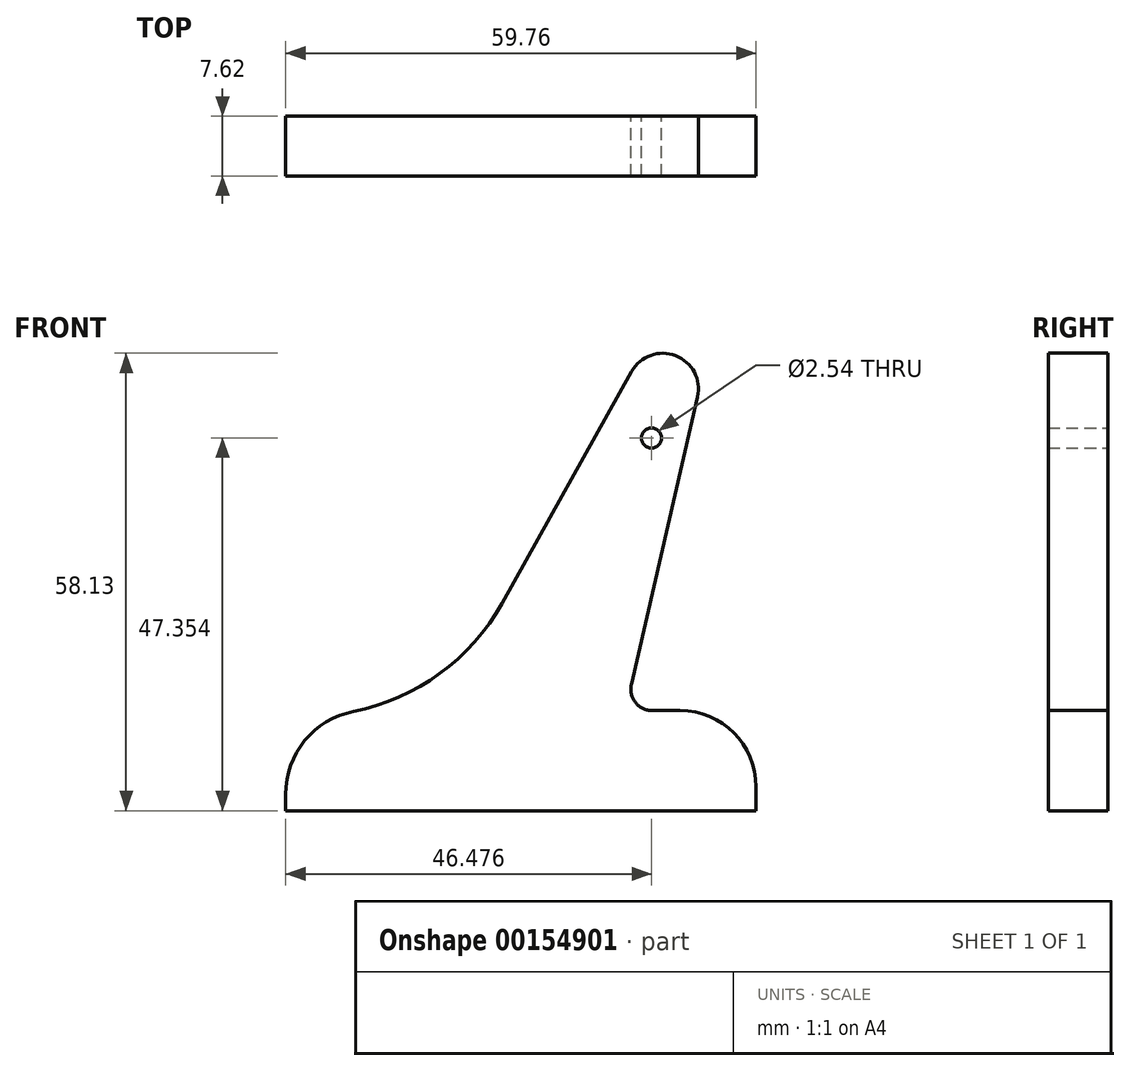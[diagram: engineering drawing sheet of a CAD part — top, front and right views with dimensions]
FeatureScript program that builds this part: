
annotation { "Feature Type Name" : "Feature", "Feature Type Description" : "" }
export const myFeature = defineFeature(function(context is Context, id is Id, definition is map)
    precondition{}
    {
        {
            var Q0;
            Q0=qCreatedBy(makeId("Front.planeOp"),FACE);
            var sketch = newSketch(context, id + "F0", { "sketchPlane" : qUnion([Q0])});
            skLineSegment(sketch, "E0", {"start": v(-31.95, 0) * mm, "end": v(0, 0) * mm});
            skLineSegment(sketch, "E1", {"start": v(0, 0) * mm, "end": v(27.81, 0) * mm});
            skLineSegment(sketch, "E2", {"start": v(-31.95, 0) * mm, "end": v(-31.95, 12.83) * mm});
            skLineSegment(sketch, "E3", {"start": v(-31.95, 12.83) * mm, "end": v(-12, 12.83) * mm});
            skLineSegment(sketch, "E4", {"start": v(-12, 12.83) * mm, "end": v(27.51, 83.55) * mm});
            skLineSegment(sketch, "E5", {"start": v(27.51, 83.55) * mm, "end": v(11.2, 12.72) * mm});
            skLineSegment(sketch, "E6", {"start": v(27.81, 0) * mm, "end": v(27.81, 12.72) * mm});
            skLineSegment(sketch, "E7", {"start": v(27.81, 12.72) * mm, "end": v(11.2, 12.72) * mm});
            skCircle(sketch, "E8", {"center": v(14.53, 47.35) * mm, "radius": 1.27 * mm});
            skSolve(sketch);
        }
        {
            var Q0;
            Q0=makeQuery(id+"F0.imprint","IMPRINT",FACE,{"disambiguationData":[TD([[makeQuery(id+"F0.imprint","IMPRINT",EDGE,{"derivedFrom":sQuery(id+"F0.wireOp",EDGE,"E0")}),1.0]])]});
            extrude(context, id + "F1", {"entities" : qUnion([Q0]), "depth" : 7.62 * mm});
        }
        {
            var Q0;
            Q0=makeQuery(id+"F1.opExtrude","SWEPT_EDGE",EDGE,{"disambiguationData":[OSD([sQuery(id+"F0.wireOp",EDGE,"E2"),sQuery(id+"F0.wireOp",EDGE,"E3")])]});
            fillet(context, id + "F2", {"entities" : qUnion([Q0]), "radius" : 10.73 * mm, "tangentPropagation" : true, "allowEdgeOverflow" : false});
        }
        {
            var Q0;
            Q0=makeQuery(id+"F1.opExtrude","SWEPT_EDGE",EDGE,{"disambiguationData":[OSD([sQuery(id+"F0.wireOp",EDGE,"E3"),sQuery(id+"F0.wireOp",EDGE,"E4")])]});
            fillet(context, id + "F3", {"entities" : qUnion([Q0]), "radius" : 27.85 * mm, "tangentPropagation" : true, "allowEdgeOverflow" : false});
        }
        {
            var Q0;
            Q0=makeQuery(id+"F1.opExtrude","SWEPT_EDGE",EDGE,{"disambiguationData":[OSD([sQuery(id+"F0.wireOp",EDGE,"E4"),sQuery(id+"F0.wireOp",EDGE,"E5")])]});
            fillet(context, id + "F4", {"entities" : qUnion([Q0]), "radius" : 4.53 * mm, "tangentPropagation" : true, "allowEdgeOverflow" : false});
        }
        {
            var Q0;
            Q0=makeQuery(id+"F1.opExtrude","SWEPT_EDGE",EDGE,{"disambiguationData":[OSD([sQuery(id+"F0.wireOp",EDGE,"E6"),sQuery(id+"F0.wireOp",EDGE,"E7")])]});
            fillet(context, id + "F5", {"entities" : qUnion([Q0]), "radius" : 9.66 * mm, "tangentPropagation" : true, "allowEdgeOverflow" : false});
        }
        {
            var Q0;
            Q0=makeQuery(id+"F1.opExtrude","SWEPT_EDGE",EDGE,{"disambiguationData":[OSD([sQuery(id+"F0.wireOp",EDGE,"E5"),sQuery(id+"F0.wireOp",EDGE,"E7")])]});
            fillet(context, id + "F6", {"entities" : qUnion([Q0]), "radius" : 2.72 * mm, "tangentPropagation" : true, "allowEdgeOverflow" : false});
        }
    });
